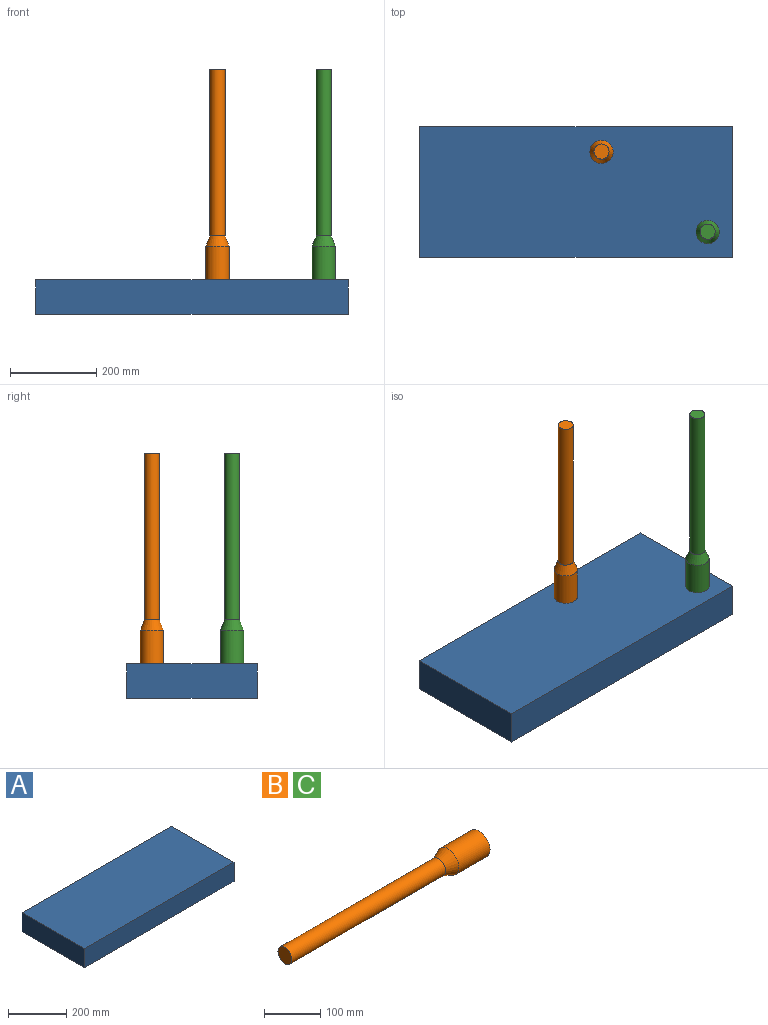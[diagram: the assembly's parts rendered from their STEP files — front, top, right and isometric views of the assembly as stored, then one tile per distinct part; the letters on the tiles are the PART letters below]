
ASSEMBLY  parts=3 mates=2
PART A: 6 faces, bbox 726.3x302x80 mm
  f0: plane 302x80mm, normal (1,0,0), area 24160mm2, adj f1,f3,f4,f5
  f1: plane 726.3x80mm, normal (0,1,0), area 58104mm2, adj f0,f2,f4,f5
  f2: plane 302x80mm, normal (-1,0,0), area 24160mm2, adj f1,f3,f4,f5
  f3: plane 726.3x80mm, normal (0,-1,0), area 58104mm2, adj f0,f2,f4,f5
  f4: plane 726.3x302mm, normal (0,0,1), area 219342.6mm2, adj f0,f1,f2,f3
  f5: plane 726.3x302mm, normal (0,0,-1), area 219342.6mm2, adj f0,f1,f2,f3
PART B: 5 faces, bbox 488x54x54 mm
  f0: plane 35x35mm, normal (-1,0,0), area 962.1mm2, adj f4
  f1: plane 54x54mm, normal (1,0,0), area 2290.2mm2, adj f2
  f2: cylinder r=27mm len=78mm, axis (1,0,0), area 13232.4mm2, adj f1,f3
  f3: cone r=17.5mm half-angle=21.6deg, axis (1,0,0), area 3608.5mm2, adj f2,f4
  f4: cylinder r=17.5mm len=386mm, axis (1,0,0), area 42442.9mm2, adj f0,f3
PART C: same geometry as B
PLACE A at identity fixed
PLACE B rot(axis=(0.71,0,-0.71),180deg) t=(59.1,93,568)mm
PLACE C rot(axis=(0.71,0,-0.71),180deg) t=(305.6,-93,568)mm
MATE fastened B.f2 <-> A.f4  axis (0,0,-1) through (59.1,93,80)mm
MATE fastened C.f2 <-> A.f4  axis (0,0,-1) through (305.6,-93,80)mm
